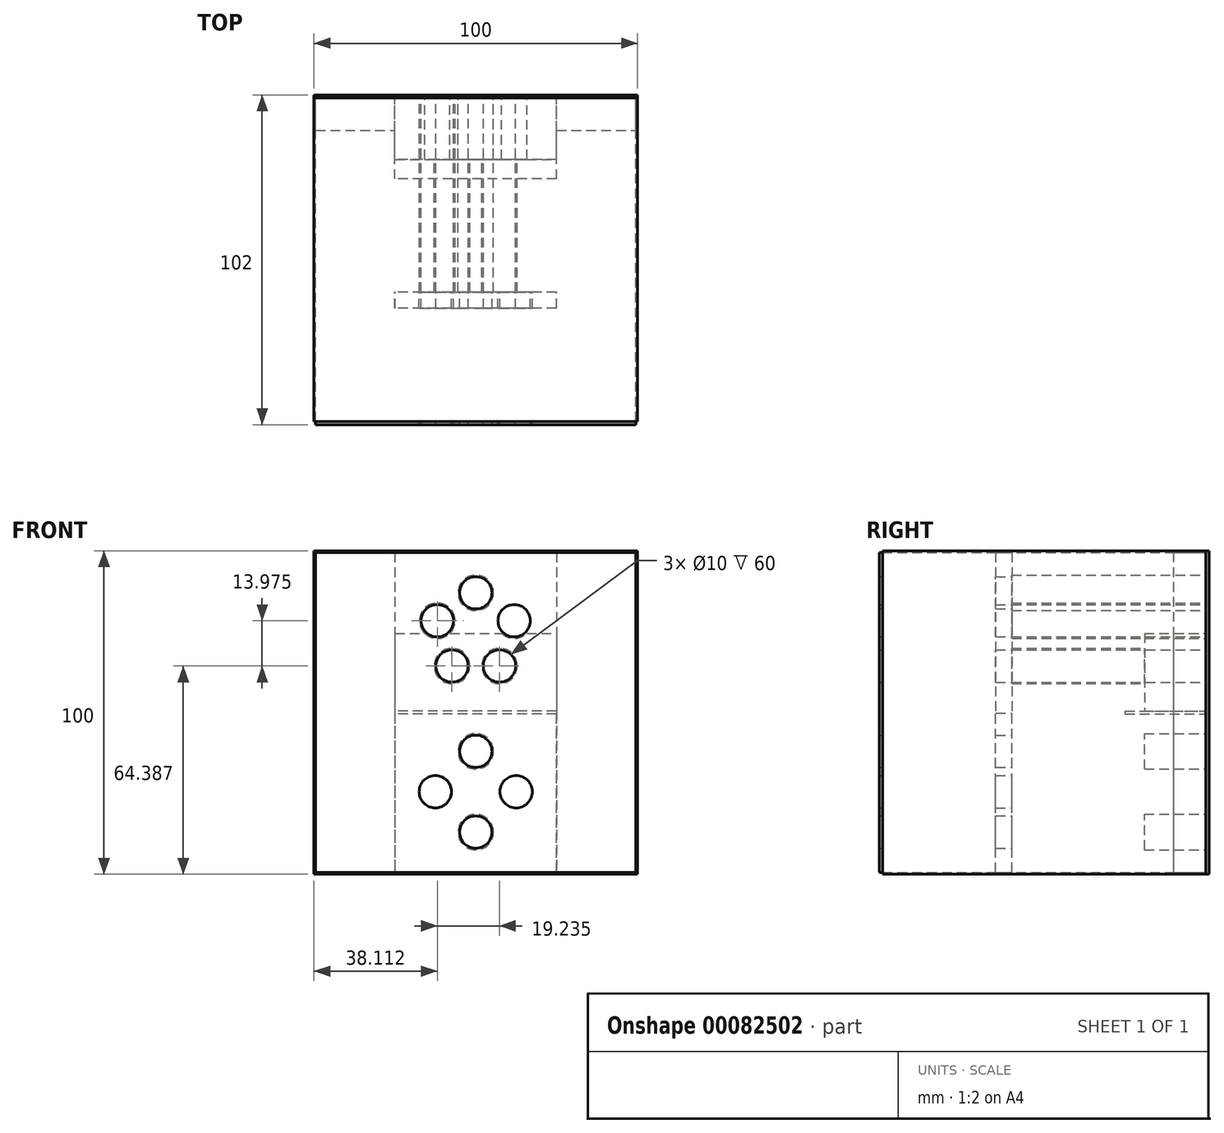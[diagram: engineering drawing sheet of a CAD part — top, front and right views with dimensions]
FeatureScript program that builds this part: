
annotation { "Feature Type Name" : "Feature", "Feature Type Description" : "" }
export const myFeature = defineFeature(function(context is Context, id is Id, definition is map)
    precondition{}
    {
        {
            var Q0;
            Q0=qCreatedBy(makeId("Front.planeOp"),FACE);
            var sketch = newSketch(context, id + "F0", { "sketchPlane" : qUnion([Q0])});
            skLineSegment(sketch, "E0.rect.bottom", {"start": v(-49.5, 49.5) * mm, "end": v(49.5, 49.5) * mm});
            skLineSegment(sketch, "E0.rect.top", {"start": v(-49.5, -49.5) * mm, "end": v(49.5, -49.5) * mm});
            skLineSegment(sketch, "E0.rect.left", {"start": v(-49.5, 49.5) * mm, "end": v(-49.5, -49.5) * mm});
            skLineSegment(sketch, "E0.rect.right", {"start": v(49.5, 49.5) * mm, "end": v(49.5, -49.5) * mm});
            skPoint(sketch, "E0.rect.middle", {"position": v(0, 0) * mm});
            skLineSegment(sketch, "E1", {"start": v(-49.5, 0) * mm, "end": v(49.5, 0) * mm});
            skLineSegment(sketch, "E2", {"start": v(0, 49.5) * mm, "end": v(0, -49.5) * mm});
            skLineSegment(sketch, "E3", {"start": v(-49.5, 24.5) * mm, "end": v(49.5, 24.5) * mm});
            skPoint(sketch, "E4", {"position": v(0, 24.5) * mm});
            skPoint(sketch, "E5", {"position": v(0, 37) * mm});
            skPoint(sketch, "E6", {"position": v(0, 12) * mm});
            skCircle(sketch, "E7", {"center": v(0, 37) * mm, "radius": 5.5 * mm});
            skPoint(sketch, "E8.1.0", {"position": v(-11.89, 28.36) * mm});
            skPoint(sketch, "E8.2.0", {"position": v(-7.35, 14.39) * mm});
            skPoint(sketch, "E8.3.0", {"position": v(7.35, 14.39) * mm});
            skCircle(sketch, "E9", {"center": v(-11.89, 28.36) * mm, "radius": 5.5 * mm});
            skCircle(sketch, "E10", {"center": v(11.89, 28.36) * mm, "radius": 5.5 * mm});
            skCircle(sketch, "E11", {"center": v(-7.35, 14.39) * mm, "radius": 5.5 * mm});
            skLineSegment(sketch, "E12", {"start": v(-49.5, -24.5) * mm, "end": v(49.5, -24.5) * mm});
            skPoint(sketch, "E13", {"position": v(0, -24.5) * mm});
            skPoint(sketch, "E14", {"position": v(0, -37) * mm});
            skPoint(sketch, "E15", {"position": v(0, -12) * mm});
            skCircle(sketch, "E16", {"center": v(7.35, 14.39) * mm, "radius": 5.5 * mm});
            skPoint(sketch, "E17.1.0", {"position": v(12.5, -24.5) * mm});
            skPoint(sketch, "E17.1.1", {"position": v(-24.5, -24.5) * mm});
            skLineSegment(sketch, "E17.1.2", {"start": v(-74, -24.5) * mm, "end": v(25, -24.5) * mm});
            skPoint(sketch, "E17.1.3", {"position": v(-12.5, -24.5) * mm});
            skPoint(sketch, "E17.2.1", {"position": v(0, -49) * mm});
            skLineSegment(sketch, "E17.2.2", {"start": v(0, -98.5) * mm, "end": v(0, 0.5) * mm});
            skPoint(sketch, "E17.3.0", {"position": v(-12.5, -24.5) * mm});
            skPoint(sketch, "E17.3.1", {"position": v(24.5, -24.5) * mm});
            skLineSegment(sketch, "E17.3.2", {"start": v(74, -24.5) * mm, "end": v(-25, -24.5) * mm});
            skPoint(sketch, "E17.3.3", {"position": v(12.5, -24.5) * mm});
            skCircle(sketch, "E18", {"center": v(-12.5, -24.5) * mm, "radius": 5.5 * mm});
            skCircle(sketch, "E19", {"center": v(0, -12) * mm, "radius": 5.5 * mm});
            skCircle(sketch, "E20", {"center": v(12.5, -24.5) * mm, "radius": 5.5 * mm});
            skCircle(sketch, "E21", {"center": v(0, -37) * mm, "radius": 5.5 * mm});
            skLineSegment(sketch, "E22.rect.bottom", {"start": v(25, 49.5) * mm, "end": v(-25, 49.5) * mm});
            skLineSegment(sketch, "E22.rect.top", {"start": v(25, -0.5) * mm, "end": v(-25, -0.5) * mm});
            skLineSegment(sketch, "E22.rect.left", {"start": v(25, 49.5) * mm, "end": v(25, -0.5) * mm});
            skLineSegment(sketch, "E22.rect.right", {"start": v(-25, 49.5) * mm, "end": v(-25, -0.5) * mm});
            skLineSegment(sketch, "E23.rect.bottom", {"start": v(25, 0.5) * mm, "end": v(-25, 0.5) * mm});
            skLineSegment(sketch, "E23.rect.top", {"start": v(25, -49.5) * mm, "end": v(-25, -49.5) * mm});
            skLineSegment(sketch, "E23.rect.left", {"start": v(25, 0.5) * mm, "end": v(25, -49.5) * mm});
            skLineSegment(sketch, "E23.rect.right", {"start": v(-25, 0.5) * mm, "end": v(-25, -49.5) * mm});
            skSolve(sketch);
        }
        {
            var Q0;
            Q0=makeQuery(id+"F0.imprint","IMPRINT",FACE,{"disambiguationData":[TD([[makeQuery(id+"F0.imprint","IMPRINT",EDGE,{"derivedFrom":sQuery(id+"F0.wireOp",EDGE,"E11")}),-1.0]])]});
            var Q1;
            {var subQ1=sQuery(id+"F0.wireOp",EDGE,"E2");var subQ8=sQuery(id+"F0.wireOp",EDGE,"E22.rect.bottom");var subQ9=makeQuery(id+"F0.imprint","INTERSECT",VERTEX,{"derivedFrom":[subQ1,subQ8]});Q1=makeQuery(id+"F0.imprint","IMPRINT",FACE,{"disambiguationData":[TD([[makeQuery(id+"F0.imprint","IMPRINT",EDGE,{"disambiguationData":[TD([[subQ9,-1.0]])],"derivedFrom":subQ1}),-1.0]])]});}
            var Q2;
            {var subQ6=sQuery(id+"F0.wireOp",EDGE,"E2");var subQ10=sQuery(id+"F0.wireOp",EDGE,"E22.rect.bottom");var subQ11=makeQuery(id+"F0.imprint","INTERSECT",VERTEX,{"derivedFrom":[subQ6,subQ10]});Q2=makeQuery(id+"F0.imprint","IMPRINT",FACE,{"disambiguationData":[TD([[makeQuery(id+"F0.imprint","IMPRINT",EDGE,{"disambiguationData":[TD([[subQ11,-1.0]])],"derivedFrom":subQ6}),1.0]])]});}
            var Q3;
            Q3=makeQuery(id+"F0.imprint","IMPRINT",FACE,{"disambiguationData":[TD([[makeQuery(id+"F0.imprint","IMPRINT",EDGE,{"derivedFrom":sQuery(id+"F0.wireOp",EDGE,"E16")}),-1.0]])]});
            var Q4;
            {var subQ0=sQuery(id+"F0.wireOp",EDGE,"E17.3.2");var subQ1=sQuery(id+"F0.wireOp",EDGE,"E17.2.2");var subQ2=makeQuery(id+"F0.imprint","INTERSECT",VERTEX,{"derivedFrom":[subQ1,subQ0]});Q4=makeQuery(id+"F0.imprint","IMPRINT",FACE,{"disambiguationData":[TD([[makeQuery(id+"F0.imprint","IMPRINT",EDGE,{"disambiguationData":[TD([[subQ2,-1.0]])],"derivedFrom":subQ1}),-1.0]])]});}
            var Q5;
            {var subQ1=sQuery(id+"F0.wireOp",EDGE,"E17.3.2");var subQ6=sQuery(id+"F0.wireOp",EDGE,"E17.2.2");var subQ10=makeQuery(id+"F0.imprint","INTERSECT",VERTEX,{"derivedFrom":[subQ6,subQ1]});Q5=makeQuery(id+"F0.imprint","IMPRINT",FACE,{"disambiguationData":[TD([[makeQuery(id+"F0.imprint","IMPRINT",EDGE,{"disambiguationData":[TD([[subQ10,-1.0]])],"derivedFrom":subQ6}),1.0]])]});}
            var Q6;
            {var subQ6=sQuery(id+"F0.wireOp",EDGE,"E17.2.2");var subQ11=sQuery(id+"F0.wireOp",EDGE,"E23.rect.top");var subQ13=makeQuery(id+"F0.imprint","INTERSECT",VERTEX,{"derivedFrom":[subQ6,subQ11]});Q6=makeQuery(id+"F0.imprint","IMPRINT",FACE,{"disambiguationData":[TD([[makeQuery(id+"F0.imprint","IMPRINT",EDGE,{"disambiguationData":[TD([[subQ13,-1.0]])],"derivedFrom":subQ6}),1.0]])]});}
            var Q7;
            {var subQ1=sQuery(id+"F0.wireOp",EDGE,"E17.2.2");var subQ10=sQuery(id+"F0.wireOp",EDGE,"E23.rect.top");var subQ11=makeQuery(id+"F0.imprint","INTERSECT",VERTEX,{"derivedFrom":[subQ1,subQ10]});Q7=makeQuery(id+"F0.imprint","IMPRINT",FACE,{"disambiguationData":[TD([[makeQuery(id+"F0.imprint","IMPRINT",EDGE,{"disambiguationData":[TD([[subQ11,-1.0]])],"derivedFrom":subQ1}),-1.0]])]});}
            extrude(context, id + "F1", {"entities" : qUnion([Q0, Q1, Q2, Q3, Q4, Q5, Q6, Q7]), "depth" : 19 * mm});
        }
        {
            var Q0;
            {var subQ0=sQuery(id+"F0.wireOp",EDGE,"E0.rect.left");var subQ1=sQuery(id+"F0.wireOp",EDGE,"E0.rect.bottom");var subQ2=makeQuery(id+"F0.imprint","INTERSECT",VERTEX,{"derivedFrom":[subQ1,subQ0]});Q0=makeQuery(id+"F0.imprint","IMPRINT",FACE,{"disambiguationData":[TD([[makeQuery(id+"F0.imprint","IMPRINT",EDGE,{"disambiguationData":[TD([[subQ2,-1.0]])],"derivedFrom":subQ0}),1.0]])]});}
            var Q1;
            {var subQ0=sQuery(id+"F0.wireOp",EDGE,"E1");var subQ1=sQuery(id+"F0.wireOp",EDGE,"E0.rect.left");var subQ2=makeQuery(id+"F0.imprint","INTERSECT",VERTEX,{"derivedFrom":[subQ1,subQ0]});Q1=makeQuery(id+"F0.imprint","IMPRINT",FACE,{"disambiguationData":[TD([[makeQuery(id+"F0.imprint","IMPRINT",EDGE,{"disambiguationData":[TD([[subQ2,1.0]])],"derivedFrom":subQ1}),1.0]])]});}
            var Q2;
            {var subQ0=sQuery(id+"F0.wireOp",EDGE,"E1");var subQ1=sQuery(id+"F0.wireOp",EDGE,"E0.rect.left");var subQ2=makeQuery(id+"F0.imprint","INTERSECT",VERTEX,{"derivedFrom":[subQ1,subQ0]});Q2=makeQuery(id+"F0.imprint","IMPRINT",FACE,{"disambiguationData":[TD([[makeQuery(id+"F0.imprint","IMPRINT",EDGE,{"disambiguationData":[TD([[subQ2,-1.0]])],"derivedFrom":subQ1}),1.0]])]});}
            var Q3;
            {var subQ0=sQuery(id+"F0.wireOp",EDGE,"E0.rect.left");var subQ1=sQuery(id+"F0.wireOp",EDGE,"E0.rect.top");var subQ2=makeQuery(id+"F0.imprint","INTERSECT",VERTEX,{"derivedFrom":[subQ1,subQ0]});Q3=makeQuery(id+"F0.imprint","IMPRINT",FACE,{"disambiguationData":[TD([[makeQuery(id+"F0.imprint","IMPRINT",EDGE,{"disambiguationData":[TD([[subQ2,1.0]])],"derivedFrom":subQ0}),1.0]])]});}
            var Q4;
            {var subQ0=sQuery(id+"F0.wireOp",EDGE,"E0.rect.right");var subQ1=sQuery(id+"F0.wireOp",EDGE,"E0.rect.top");var subQ2=makeQuery(id+"F0.imprint","INTERSECT",VERTEX,{"derivedFrom":[subQ1,subQ0]});Q4=makeQuery(id+"F0.imprint","IMPRINT",FACE,{"disambiguationData":[TD([[makeQuery(id+"F0.imprint","IMPRINT",EDGE,{"disambiguationData":[TD([[subQ2,1.0]])],"derivedFrom":subQ0}),-1.0]])]});}
            var Q5;
            {var subQ0=sQuery(id+"F0.wireOp",EDGE,"E1");var subQ1=sQuery(id+"F0.wireOp",EDGE,"E0.rect.right");var subQ2=makeQuery(id+"F0.imprint","INTERSECT",VERTEX,{"derivedFrom":[subQ1,subQ0]});Q5=makeQuery(id+"F0.imprint","IMPRINT",FACE,{"disambiguationData":[TD([[makeQuery(id+"F0.imprint","IMPRINT",EDGE,{"disambiguationData":[TD([[subQ2,-1.0]])],"derivedFrom":subQ1}),-1.0]])]});}
            var Q6;
            {var subQ0=sQuery(id+"F0.wireOp",EDGE,"E1");var subQ1=sQuery(id+"F0.wireOp",EDGE,"E0.rect.right");var subQ2=makeQuery(id+"F0.imprint","INTERSECT",VERTEX,{"derivedFrom":[subQ1,subQ0]});Q6=makeQuery(id+"F0.imprint","IMPRINT",FACE,{"disambiguationData":[TD([[makeQuery(id+"F0.imprint","IMPRINT",EDGE,{"disambiguationData":[TD([[subQ2,1.0]])],"derivedFrom":subQ1}),-1.0]])]});}
            var Q7;
            {var subQ0=sQuery(id+"F0.wireOp",EDGE,"E0.rect.right");var subQ1=sQuery(id+"F0.wireOp",EDGE,"E0.rect.bottom");var subQ2=makeQuery(id+"F0.imprint","INTERSECT",VERTEX,{"derivedFrom":[subQ1,subQ0]});Q7=makeQuery(id+"F0.imprint","IMPRINT",FACE,{"disambiguationData":[TD([[makeQuery(id+"F0.imprint","IMPRINT",EDGE,{"disambiguationData":[TD([[subQ2,-1.0]])],"derivedFrom":subQ0}),-1.0]])]});}
            extrude(context, id + "F2", {"entities" : qUnion([Q0, Q1, Q2, Q3, Q4, Q5, Q6, Q7]), "operationType" : NewBodyOperationType.ADD, "depth" : 10 * mm});
        }
        {
            var Q0;
            {var subQ0=sQuery(id+"F0.wireOp",EDGE,"E9");var subQ1=sQuery(id+"F0.wireOp",EDGE,"E3");var subQ2=makeQuery(id+"F0.imprint","INTERSECT",VERTEX,{"disambiguationData":[OD(0.0)],"derivedFrom":[subQ1,subQ0]});Q0=makeQuery(id+"F0.imprint","IMPRINT",FACE,{"disambiguationData":[TD([[makeQuery(id+"F0.imprint","IMPRINT",EDGE,{"disambiguationData":[TD([[subQ2,-1.0]])],"derivedFrom":subQ1}),1.0]])]});}
            var Q1;
            {var subQ0=sQuery(id+"F0.wireOp",EDGE,"E9");var subQ1=sQuery(id+"F0.wireOp",EDGE,"E3");var subQ2=makeQuery(id+"F0.imprint","INTERSECT",VERTEX,{"disambiguationData":[OD(0.0)],"derivedFrom":[subQ1,subQ0]});Q1=makeQuery(id+"F0.imprint","IMPRINT",FACE,{"disambiguationData":[TD([[makeQuery(id+"F0.imprint","IMPRINT",EDGE,{"disambiguationData":[TD([[subQ2,-1.0]])],"derivedFrom":subQ1}),-1.0]])]});}
            var Q2;
            {var subQ0=sQuery(id+"F0.wireOp",EDGE,"E7");var subQ1=sQuery(id+"F0.wireOp",EDGE,"E2");var subQ2=makeQuery(id+"F0.imprint","INTERSECT",VERTEX,{"disambiguationData":[OD(0.0)],"derivedFrom":[subQ1,subQ0]});Q2=makeQuery(id+"F0.imprint","IMPRINT",FACE,{"disambiguationData":[TD([[makeQuery(id+"F0.imprint","IMPRINT",EDGE,{"disambiguationData":[TD([[subQ2,-1.0]])],"derivedFrom":subQ1}),1.0]])]});}
            var Q3;
            {var subQ0=sQuery(id+"F0.wireOp",EDGE,"E7");var subQ1=sQuery(id+"F0.wireOp",EDGE,"E2");var subQ2=makeQuery(id+"F0.imprint","INTERSECT",VERTEX,{"disambiguationData":[OD(0.0)],"derivedFrom":[subQ1,subQ0]});Q3=makeQuery(id+"F0.imprint","IMPRINT",FACE,{"disambiguationData":[TD([[makeQuery(id+"F0.imprint","IMPRINT",EDGE,{"disambiguationData":[TD([[subQ2,-1.0]])],"derivedFrom":subQ1}),-1.0]])]});}
            var Q4;
            Q4=makeQuery(id+"F0.imprint","IMPRINT",FACE,{"disambiguationData":[TD([[makeQuery(id+"F0.imprint","IMPRINT",EDGE,{"derivedFrom":sQuery(id+"F0.wireOp",EDGE,"E16")}),1.0]])]});
            var Q5;
            Q5=makeQuery(id+"F0.imprint","IMPRINT",FACE,{"disambiguationData":[TD([[makeQuery(id+"F0.imprint","IMPRINT",EDGE,{"derivedFrom":sQuery(id+"F0.wireOp",EDGE,"E11")}),1.0]])]});
            var Q6;
            {var subQ0=sQuery(id+"F0.wireOp",EDGE,"E19");var subQ1=sQuery(id+"F0.wireOp",EDGE,"E17.2.2");var subQ2=makeQuery(id+"F0.imprint","INTERSECT",VERTEX,{"disambiguationData":[OD(0.0)],"derivedFrom":[subQ1,subQ0]});Q6=makeQuery(id+"F0.imprint","IMPRINT",FACE,{"disambiguationData":[TD([[makeQuery(id+"F0.imprint","IMPRINT",EDGE,{"disambiguationData":[TD([[subQ2,-1.0]])],"derivedFrom":subQ1}),-1.0]])]});}
            var Q7;
            {var subQ0=sQuery(id+"F0.wireOp",EDGE,"E19");var subQ1=sQuery(id+"F0.wireOp",EDGE,"E17.2.2");var subQ2=makeQuery(id+"F0.imprint","INTERSECT",VERTEX,{"disambiguationData":[OD(0.0)],"derivedFrom":[subQ1,subQ0]});Q7=makeQuery(id+"F0.imprint","IMPRINT",FACE,{"disambiguationData":[TD([[makeQuery(id+"F0.imprint","IMPRINT",EDGE,{"disambiguationData":[TD([[subQ2,-1.0]])],"derivedFrom":subQ1}),1.0]])]});}
            var Q8;
            {var subQ0=sQuery(id+"F0.wireOp",EDGE,"E18");var subQ1=sQuery(id+"F0.wireOp",EDGE,"E17.3.2");var subQ2=makeQuery(id+"F0.imprint","INTERSECT",VERTEX,{"disambiguationData":[OD(0.0)],"derivedFrom":[subQ1,subQ0]});Q8=makeQuery(id+"F0.imprint","IMPRINT",FACE,{"disambiguationData":[TD([[makeQuery(id+"F0.imprint","IMPRINT",EDGE,{"disambiguationData":[TD([[subQ2,-1.0]])],"derivedFrom":subQ1}),-1.0]])]});}
            var Q9;
            {var subQ0=sQuery(id+"F0.wireOp",EDGE,"E18");var subQ1=sQuery(id+"F0.wireOp",EDGE,"E17.3.2");var subQ2=makeQuery(id+"F0.imprint","INTERSECT",VERTEX,{"disambiguationData":[OD(0.0)],"derivedFrom":[subQ1,subQ0]});Q9=makeQuery(id+"F0.imprint","IMPRINT",FACE,{"disambiguationData":[TD([[makeQuery(id+"F0.imprint","IMPRINT",EDGE,{"disambiguationData":[TD([[subQ2,-1.0]])],"derivedFrom":subQ1}),1.0]])]});}
            var Q10;
            {var subQ0=sQuery(id+"F0.wireOp",EDGE,"E20");var subQ1=sQuery(id+"F0.wireOp",EDGE,"E17.3.2");var subQ2=makeQuery(id+"F0.imprint","INTERSECT",VERTEX,{"disambiguationData":[OD(0.0)],"derivedFrom":[subQ1,subQ0]});Q10=makeQuery(id+"F0.imprint","IMPRINT",FACE,{"disambiguationData":[TD([[makeQuery(id+"F0.imprint","IMPRINT",EDGE,{"disambiguationData":[TD([[subQ2,-1.0]])],"derivedFrom":subQ1}),-1.0]])]});}
            var Q11;
            {var subQ0=sQuery(id+"F0.wireOp",EDGE,"E20");var subQ1=sQuery(id+"F0.wireOp",EDGE,"E17.3.2");var subQ2=makeQuery(id+"F0.imprint","INTERSECT",VERTEX,{"disambiguationData":[OD(0.0)],"derivedFrom":[subQ1,subQ0]});Q11=makeQuery(id+"F0.imprint","IMPRINT",FACE,{"disambiguationData":[TD([[makeQuery(id+"F0.imprint","IMPRINT",EDGE,{"disambiguationData":[TD([[subQ2,-1.0]])],"derivedFrom":subQ1}),1.0]])]});}
            var Q12;
            {var subQ0=sQuery(id+"F0.wireOp",EDGE,"E21");var subQ1=sQuery(id+"F0.wireOp",EDGE,"E17.2.2");var subQ2=makeQuery(id+"F0.imprint","INTERSECT",VERTEX,{"disambiguationData":[OD(0.0)],"derivedFrom":[subQ1,subQ0]});Q12=makeQuery(id+"F0.imprint","IMPRINT",FACE,{"disambiguationData":[TD([[makeQuery(id+"F0.imprint","IMPRINT",EDGE,{"disambiguationData":[TD([[subQ2,-1.0]])],"derivedFrom":subQ1}),-1.0]])]});}
            var Q13;
            {var subQ0=sQuery(id+"F0.wireOp",EDGE,"E21");var subQ1=sQuery(id+"F0.wireOp",EDGE,"E17.2.2");var subQ2=makeQuery(id+"F0.imprint","INTERSECT",VERTEX,{"disambiguationData":[OD(0.0)],"derivedFrom":[subQ1,subQ0]});Q13=makeQuery(id+"F0.imprint","IMPRINT",FACE,{"disambiguationData":[TD([[makeQuery(id+"F0.imprint","IMPRINT",EDGE,{"disambiguationData":[TD([[subQ2,-1.0]])],"derivedFrom":subQ1}),1.0]])]});}
            var Q14;
            {var subQ0=sQuery(id+"F0.wireOp",EDGE,"da757bd1-b4bc-44ba-8823-31735c9c6de2");var subQ1=sQuery(id+"F0.wireOp",EDGE,"E3");var subQ2=makeQuery(id+"F0.imprint","INTERSECT",VERTEX,{"disambiguationData":[OD(0.0)],"derivedFrom":[subQ1,subQ0]});Q14=makeQuery(id+"F0.imprint","IMPRINT",FACE,{"disambiguationData":[TD([[makeQuery(id+"F0.imprint","IMPRINT",EDGE,{"disambiguationData":[TD([[subQ2,-1.0]])],"derivedFrom":subQ1}),-1.0]])]});}
            var Q15;
            {var subQ0=sQuery(id+"F0.wireOp",EDGE,"da757bd1-b4bc-44ba-8823-31735c9c6de2");var subQ1=sQuery(id+"F0.wireOp",EDGE,"E3");var subQ2=makeQuery(id+"F0.imprint","INTERSECT",VERTEX,{"disambiguationData":[OD(0.0)],"derivedFrom":[subQ1,subQ0]});Q15=makeQuery(id+"F0.imprint","IMPRINT",FACE,{"disambiguationData":[TD([[makeQuery(id+"F0.imprint","IMPRINT",EDGE,{"disambiguationData":[TD([[subQ2,-1.0]])],"derivedFrom":subQ1}),1.0]])]});}
            extrude(context, id + "F3", {"entities" : qUnion([Q0, Q1, Q2, Q3, Q4, Q5, Q6, Q7, Q8, Q9, Q10, Q11, Q12, Q13, Q14, Q15]), "operationType" : NewBodyOperationType.ADD, "depth" : 60 * mm});
        }
        {
            var Q0;
            {var subQ0=sQuery(id+"F0.wireOp",EDGE,"E23.rect.right");var subQ1=sQuery(id+"F0.wireOp",EDGE,"E1");var subQ2=makeQuery(id+"F0.imprint","INTERSECT",VERTEX,{"derivedFrom":[subQ1,subQ0]});Q0=makeQuery(id+"F0.imprint","IMPRINT",FACE,{"disambiguationData":[TD([[makeQuery(id+"F0.imprint","IMPRINT",EDGE,{"disambiguationData":[TD([[subQ2,-1.0]])],"derivedFrom":subQ1}),-1.0]])]});}
            var Q1;
            {var subQ0=sQuery(id+"F0.wireOp",EDGE,"E23.rect.right");var subQ1=sQuery(id+"F0.wireOp",EDGE,"E1");var subQ2=makeQuery(id+"F0.imprint","INTERSECT",VERTEX,{"derivedFrom":[subQ1,subQ0]});Q1=makeQuery(id+"F0.imprint","IMPRINT",FACE,{"disambiguationData":[TD([[makeQuery(id+"F0.imprint","IMPRINT",EDGE,{"disambiguationData":[TD([[subQ2,-1.0]])],"derivedFrom":subQ1}),1.0]])]});}
            var Q2;
            {var subQ0=sQuery(id+"F0.wireOp",EDGE,"E17.2.2");var subQ1=sQuery(id+"F0.wireOp",EDGE,"E1");var subQ2=makeQuery(id+"F0.imprint","INTERSECT",VERTEX,{"derivedFrom":[subQ1,subQ0]});Q2=makeQuery(id+"F0.imprint","IMPRINT",FACE,{"disambiguationData":[TD([[makeQuery(id+"F0.imprint","IMPRINT",EDGE,{"disambiguationData":[TD([[subQ2,-1.0]])],"derivedFrom":subQ1}),1.0]])]});}
            var Q3;
            {var subQ0=sQuery(id+"F0.wireOp",EDGE,"E17.2.2");var subQ1=sQuery(id+"F0.wireOp",EDGE,"E1");var subQ2=makeQuery(id+"F0.imprint","INTERSECT",VERTEX,{"derivedFrom":[subQ1,subQ0]});Q3=makeQuery(id+"F0.imprint","IMPRINT",FACE,{"disambiguationData":[TD([[makeQuery(id+"F0.imprint","IMPRINT",EDGE,{"disambiguationData":[TD([[subQ2,-1.0]])],"derivedFrom":subQ1}),-1.0]])]});}
            extrude(context, id + "F4", {"entities" : qUnion([Q0, Q1, Q2, Q3]), "depth" : 25 * mm});
        }
        {
            var Q0;
            Q0=sQuery(id+"F0.wireOp",VERTEX,"E8.1.0");
            var Q1;
            Q1=sQuery(id+"F0.wireOp",VERTEX,"E5");
            var Q2;
            Q2=sQuery(id+"F0.wireOp",VERTEX,"E10.center");
            var Q3;
            Q3=sQuery(id+"F0.wireOp",VERTEX,"E8.3.0");
            var Q4;
            Q4=sQuery(id+"F0.wireOp",VERTEX,"E8.2.0");
            var Q5;
            Q5=sQuery(id+"F0.wireOp",VERTEX,"E15");
            var Q6;
            Q6=sQuery(id+"F0.wireOp",VERTEX,"E17.1.3");
            var Q7;
            Q7=sQuery(id+"F0.wireOp",VERTEX,"E14");
            var Q8;
            Q8=sQuery(id+"F0.wireOp",VERTEX,"E17.3.3");
            var Q9;
            Q9=makeQuery(id+"F1.opExtrude","SWEPT_BODY",BODY,{"disambiguationData":[OSD([sQuery(id+"F0.wireOp",EDGE,"E7"),sQuery(id+"F0.wireOp",EDGE,"E9"),sQuery(id+"F0.wireOp",EDGE,"E10"),sQuery(id+"F0.wireOp",EDGE,"E11"),sQuery(id+"F0.wireOp",EDGE,"E16"),sQuery(id+"F0.wireOp",EDGE,"E22.rect.bottom"),sQuery(id+"F0.wireOp",EDGE,"E22.rect.left"),sQuery(id+"F0.wireOp",EDGE,"E22.rect.right"),sQuery(id+"F0.wireOp",EDGE,"E23.rect.bottom")])]});
            var Q10;
            Q10=makeQuery(id+"F3.opExtrude","SWEPT_BODY",BODY,{"disambiguationData":[OSD([sQuery(id+"F0.wireOp",EDGE,"da757bd1-b4bc-44ba-8823-31735c9c6de2")])]});
            var Q11;
            Q11=makeQuery(id+"F3.opExtrude","SWEPT_BODY",BODY,{"disambiguationData":[OSD([sQuery(id+"F0.wireOp",EDGE,"E19")])]});
            var Q12;
            Q12=makeQuery(id+"F3.opExtrude","SWEPT_BODY",BODY,{"disambiguationData":[OSD([sQuery(id+"F0.wireOp",EDGE,"E18")])]});
            var Q13;
            Q13=makeQuery(id+"F3.opExtrude","SWEPT_BODY",BODY,{"disambiguationData":[OSD([sQuery(id+"F0.wireOp",EDGE,"E21")])]});
            var Q14;
            Q14=makeQuery(id+"F3.opExtrude","SWEPT_BODY",BODY,{"disambiguationData":[OSD([sQuery(id+"F0.wireOp",EDGE,"E20")])]});
            hole(context, id + "F5", {"style" : HoleStyle.SIMPLE, "holeDiameter" : 10 * mm, "endStyle" : HoleEndStyle.THROUGH, "oppositeDirection" : true, "locations" : qUnion([Q0, Q1, Q2, Q3, Q4, Q5, Q6, Q7, Q8]), "scope" : qUnion([Q9, Q10, Q11, Q12, Q13, Q14])});
        }
        {
            var Q0;
            Q0=qCreatedBy(makeId("Front.planeOp"),FACE);
            var sketch = newSketch(context, id + "F6", { "sketchPlane" : qUnion([Q0])});
            skLineSegment(sketch, "E24.rect.bottom", {"start": v(50, 50) * mm, "end": v(-50, 50) * mm});
            skLineSegment(sketch, "E24.rect.top", {"start": v(50, -50) * mm, "end": v(-50, -50) * mm});
            skLineSegment(sketch, "E24.rect.left", {"start": v(50, 50) * mm, "end": v(50, -50) * mm});
            skLineSegment(sketch, "E24.rect.right", {"start": v(-50, 50) * mm, "end": v(-50, -50) * mm});
            skPoint(sketch, "E24.rect.middle", {"position": v(0, 0) * mm});
            skLineSegment(sketch, "E25.rect.bottom", {"start": v(49.5, -49.5) * mm, "end": v(-49.5, -49.5) * mm});
            skLineSegment(sketch, "E25.rect.top", {"start": v(49.5, 49.5) * mm, "end": v(-49.5, 49.5) * mm});
            skLineSegment(sketch, "E25.rect.left", {"start": v(49.5, -49.5) * mm, "end": v(49.5, 49.5) * mm});
            skLineSegment(sketch, "E25.rect.right", {"start": v(-49.5, -49.5) * mm, "end": v(-49.5, 49.5) * mm});
            skSolve(sketch);
        }
        {
            var Q0;
            Q0=qSketchRegion(id+"F6",true);
            extrude(context, id + "F7", {"entities" : qUnion([Q0]), "depth" : 100 * mm});
        }
        {
            var Q0;
            Q0=makeQuery(id+"F7.opExtrude","CAP_FACE",FACE,{"disambiguationData":[OSD([sQuery(id+"F6.wireOp",EDGE,"E24.rect.bottom"),sQuery(id+"F6.wireOp",EDGE,"E24.rect.top"),sQuery(id+"F6.wireOp",EDGE,"E24.rect.left"),sQuery(id+"F6.wireOp",EDGE,"E24.rect.right"),sQuery(id+"F6.wireOp",EDGE,"E25.rect.bottom"),sQuery(id+"F6.wireOp",EDGE,"E25.rect.top"),sQuery(id+"F6.wireOp",EDGE,"E25.rect.left"),sQuery(id+"F6.wireOp",EDGE,"E25.rect.right")])],"isStart":false});
            var sketch = newSketch(context, id + "F8", { "sketchPlane" : qUnion([Q0])});
            skLineSegment(sketch, "E26.rect.bottom", {"start": v(49.5, 49.5) * mm, "end": v(-49.5, 49.5) * mm});
            skLineSegment(sketch, "E26.rect.top", {"start": v(49.5, -49.5) * mm, "end": v(-49.5, -49.5) * mm});
            skLineSegment(sketch, "E26.rect.left", {"start": v(49.5, 49.5) * mm, "end": v(49.5, -49.5) * mm});
            skLineSegment(sketch, "E26.rect.right", {"start": v(-49.5, 49.5) * mm, "end": v(-49.5, -49.5) * mm});
            skPoint(sketch, "E26.rect.middle", {"position": v(0, 0) * mm});
            skCircle(sketch, "E27", {"center": v(-11.89, 28.36) * mm, "radius": 5 * mm});
            skCircle(sketch, "E28", {"center": v(0, 37) * mm, "radius": 5 * mm});
            skCircle(sketch, "E29", {"center": v(11.89, 28.36) * mm, "radius": 5 * mm});
            skCircle(sketch, "E30", {"center": v(7.35, 14.39) * mm, "radius": 5 * mm});
            skCircle(sketch, "E31", {"center": v(-7.35, 14.39) * mm, "radius": 5 * mm});
            skCircle(sketch, "E32", {"center": v(-12.5, -24.5) * mm, "radius": 5 * mm});
            skCircle(sketch, "E33", {"center": v(0, -12) * mm, "radius": 5 * mm});
            skCircle(sketch, "E34", {"center": v(12.5, -24.5) * mm, "radius": 5 * mm});
            skCircle(sketch, "E35", {"center": v(0, -37) * mm, "radius": 5 * mm});
            skSolve(sketch);
        }
        {
            var Q0;
            Q0=qSketchRegion(id+"F8",true);
            extrude(context, id + "F9", {"entities" : qUnion([Q0]), "depth" : 1 * mm});
        }
        {
            var Q0;
            Q0=qCreatedBy(makeId("Front.planeOp"),FACE);
            var sketch = newSketch(context, id + "F10", { "sketchPlane" : qUnion([Q0])});
            skLineSegment(sketch, "E36.rect.bottom", {"start": v(-50, 50) * mm, "end": v(50, 50) * mm});
            skLineSegment(sketch, "E36.rect.top", {"start": v(-50, -50) * mm, "end": v(50, -50) * mm});
            skLineSegment(sketch, "E36.rect.left", {"start": v(-50, 50) * mm, "end": v(-50, -50) * mm});
            skLineSegment(sketch, "E36.rect.right", {"start": v(50, 50) * mm, "end": v(50, -50) * mm});
            skPoint(sketch, "E36.rect.middle", {"position": v(0, 0) * mm});
            skSolve(sketch);
        }
        {
            var Q0;
            Q0=qSketchRegion(id+"F10",true);
            extrude(context, id + "F11", {"entities" : qUnion([Q0]), "oppositeDirection" : true, "depth" : 1 * mm});
        }
        {
            var Q0;
            Q0=qCreatedBy(makeId("Front.planeOp"),FACE);
            cPlane(context, id + "F12", {"entities" : qUnion([Q0]), "cplaneType" : CPlaneType.OFFSET, "offset" : 60 * mm, "width" : 150 * mm, "height" : 150 * mm});
        }
        {
            var Q0;
            Q0=qCreatedBy(id+"F12.planeOp",FACE);
            var sketch = newSketch(context, id + "F13", { "sketchPlane" : qUnion([Q0])});
            skLineSegment(sketch, "E37.rect.bottom", {"start": v(24.98, 49.47) * mm, "end": v(-24.98, 49.47) * mm});
            skLineSegment(sketch, "E37.rect.top", {"start": v(24.98, -0.2) * mm, "end": v(-24.98, -0.2) * mm});
            skLineSegment(sketch, "E37.rect.left", {"start": v(24.98, 49.47) * mm, "end": v(24.98, -0.2) * mm});
            skLineSegment(sketch, "E37.rect.right", {"start": v(-24.98, 49.47) * mm, "end": v(-24.98, -0.2) * mm});
            skPoint(sketch, "E37.rect.middle", {"position": v(0, 24.63) * mm});
            skLineSegment(sketch, "E38.rect.bottom", {"start": v(24.96, -49.47) * mm, "end": v(-24.96, -49.47) * mm});
            skLineSegment(sketch, "E38.rect.top", {"start": v(24.96, 0.69) * mm, "end": v(-24.96, 0.69) * mm});
            skLineSegment(sketch, "E38.rect.left", {"start": v(24.96, -49.47) * mm, "end": v(24.96, 0.69) * mm});
            skLineSegment(sketch, "E38.rect.right", {"start": v(-24.96, -49.47) * mm, "end": v(-24.96, 0.69) * mm});
            skPoint(sketch, "E38.rect.middle", {"position": v(0, -24.4) * mm});
            skCircle(sketch, "E39", {"center": v(-12.5, -24.5) * mm, "radius": 5 * mm});
            skCircle(sketch, "E40", {"center": v(0, -12) * mm, "radius": 5 * mm});
            skCircle(sketch, "E41", {"center": v(12.5, -24.5) * mm, "radius": 5 * mm});
            skCircle(sketch, "E42", {"center": v(0, -36.99) * mm, "radius": 5 * mm});
            skCircle(sketch, "E43", {"center": v(0, 37) * mm, "radius": 5 * mm});
            skCircle(sketch, "E44", {"center": v(11.89, 28.36) * mm, "radius": 5 * mm});
            skCircle(sketch, "E45", {"center": v(7.35, 14.39) * mm, "radius": 5 * mm});
            skCircle(sketch, "E46", {"center": v(-7.35, 14.39) * mm, "radius": 5 * mm});
            skCircle(sketch, "E47", {"center": v(-11.89, 28.36) * mm, "radius": 5 * mm});
            skSolve(sketch);
        }
        {
            var Q0;
            Q0=qSketchRegion(id+"F13",true);
            extrude(context, id + "F14", {"entities" : qUnion([Q0]), "depth" : 5 * mm});
        }
    });
